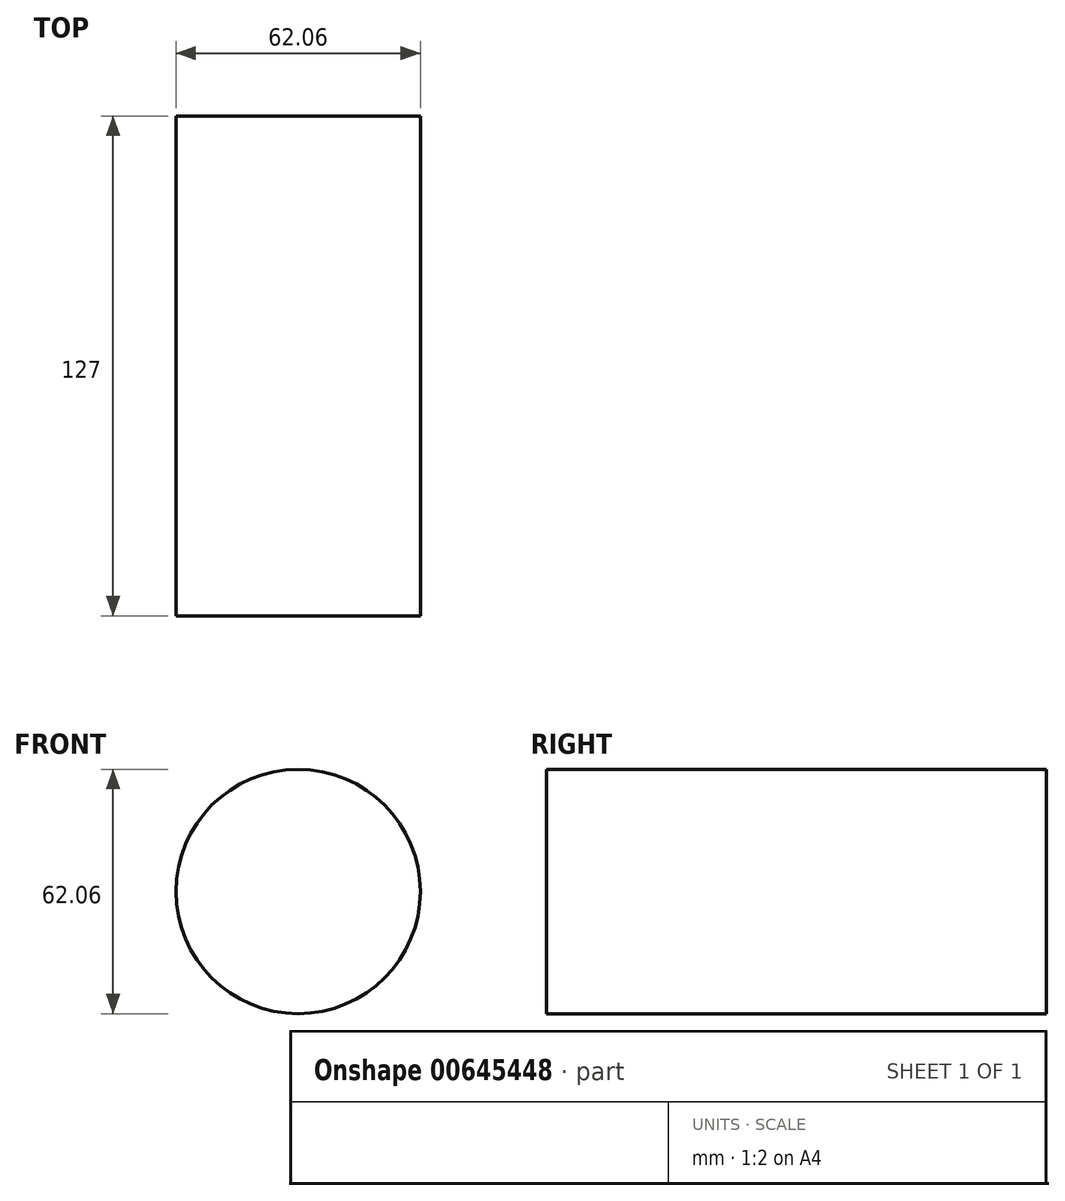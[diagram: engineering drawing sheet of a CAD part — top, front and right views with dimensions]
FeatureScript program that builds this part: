
annotation { "Feature Type Name" : "Feature", "Feature Type Description" : "" }
export const myFeature = defineFeature(function(context is Context, id is Id, definition is map)
    precondition{}
    {
        {
            var Q0;
            Q0=qCreatedBy(makeId("Front.planeOp"),FACE);
            var sketch = newSketch(context, id + "F0", { "sketchPlane" : qUnion([Q0])});
            skCircle(sketch, "E0", {"center": v(0, 0) * mm, "radius": 31.03 * mm});
            skSolve(sketch);
        }
        {
            var Q0;
            Q0=makeQuery(id+"F0.imprint","IMPRINT",FACE,{"disambiguationData":[TD([[makeQuery(id+"F0.imprint","IMPRINT",EDGE,{"derivedFrom":sQuery(id+"F0.wireOp",EDGE,"E0")}),1.0]])]});
            extrude(context, id + "F1", {"entities" : qUnion([Q0]), "depth" : 127 * mm, "offsetDistance" : 25.4 * mm});
        }
    });
